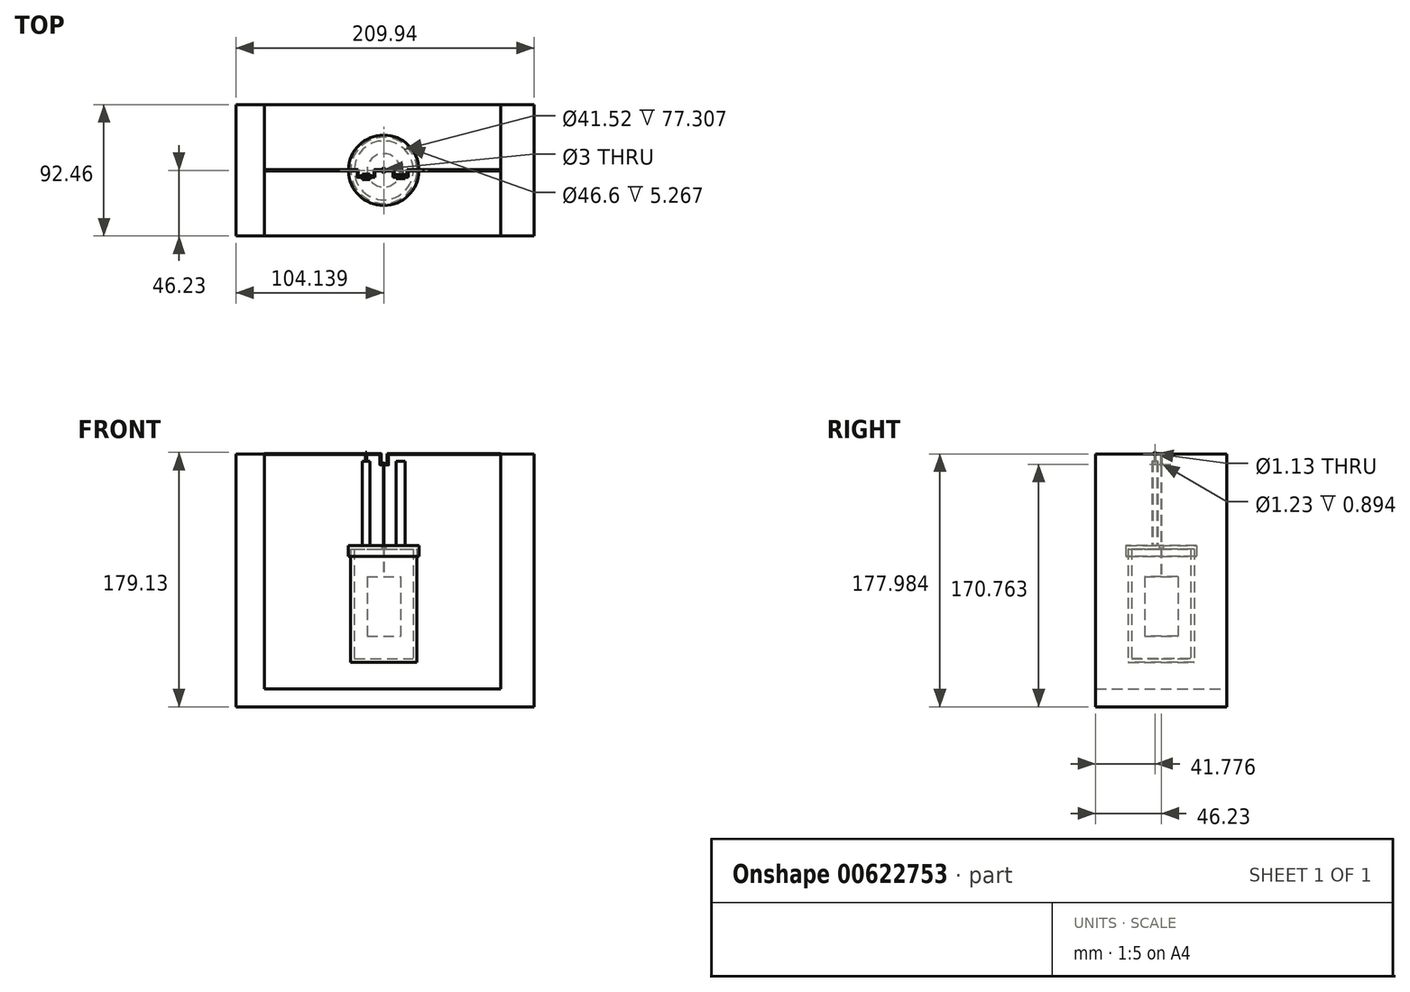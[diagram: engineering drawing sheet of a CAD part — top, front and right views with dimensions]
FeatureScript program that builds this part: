
annotation { "Feature Type Name" : "Feature", "Feature Type Description" : "" }
export const myFeature = defineFeature(function(context is Context, id is Id, definition is map)
    precondition{}
    {
        {
            var Q0;
            Q0=qCreatedBy(makeId("Front.planeOp"),FACE);
            var sketch = newSketch(context, id + "F0", { "sketchPlane" : qUnion([Q0])});
            skLineSegment(sketch, "E0.bottom", {"start": v(0, 0) * mm, "end": v(46.6, 0) * mm});
            skLineSegment(sketch, "E0.top", {"start": v(-1.54, 82.39) * mm, "end": v(43.64, 82.39) * mm});
            skLineSegment(sketch, "E0.left", {"start": v(0, 0) * mm, "end": v(0, 79.85) * mm});
            skLineSegment(sketch, "E0.right", {"start": v(46.6, 0) * mm, "end": v(46.6, 79.85) * mm});
            skLineSegment(sketch, "E1.0", {"start": v(2.54, 79.85) * mm, "end": v(44.06, 79.85) * mm});
            skLineSegment(sketch, "E1.1", {"start": v(2.54, 2.54) * mm, "end": v(2.54, 79.85) * mm});
            skLineSegment(sketch, "E1.2", {"start": v(2.54, 2.54) * mm, "end": v(44.06, 2.54) * mm});
            skLineSegment(sketch, "E1.3", {"start": v(44.06, 2.54) * mm, "end": v(44.06, 79.85) * mm});
            skLineSegment(sketch, "E2", {"start": v(21.8, 79.85) * mm, "end": v(21.8, 82.39) * mm});
            skLineSegment(sketch, "E3", {"start": v(25.2, 79.85) * mm, "end": v(25.2, 82.39) * mm});
            skLineSegment(sketch, "E4.bottom", {"start": v(11.55, 60.37) * mm, "end": v(35.83, 60.37) * mm});
            skLineSegment(sketch, "E4.top", {"start": v(11.55, 18.32) * mm, "end": v(35.83, 18.32) * mm});
            skLineSegment(sketch, "E4.left", {"start": v(11.55, 60.37) * mm, "end": v(11.55, 18.32) * mm});
            skLineSegment(sketch, "E4.right", {"start": v(35.83, 60.37) * mm, "end": v(35.83, 18.32) * mm});
            skLineSegment(sketch, "E5", {"start": v(23.1, 60.37) * mm, "end": v(23.1, 138.5) * mm});
            skLineSegment(sketch, "E6", {"start": v(23.5, 60.37) * mm, "end": v(23.5, 138.5) * mm});
            skLineSegment(sketch, "E7", {"start": v(23.5, 138.5) * mm, "end": v(23.1, 138.5) * mm});
            skLineSegment(sketch, "E8", {"start": v(2.54, 79.85) * mm, "end": v(0, 79.85) * mm});
            skLineSegment(sketch, "E9", {"start": v(44.06, 79.85) * mm, "end": v(46.6, 79.85) * mm});
            skLineSegment(sketch, "E10", {"start": v(-1.54, 82.39) * mm, "end": v(-1.54, 74.58) * mm});
            skLineSegment(sketch, "E11", {"start": v(-1.54, 74.58) * mm, "end": v(0, 74.58) * mm});
            skLineSegment(sketch, "E12", {"start": v(43.64, 82.39) * mm, "end": v(49.58, 82.39) * mm});
            skLineSegment(sketch, "E13", {"start": v(49.58, 82.39) * mm, "end": v(49.58, 75.33) * mm});
            skLineSegment(sketch, "E14", {"start": v(49.58, 75.33) * mm, "end": v(46.6, 75.33) * mm});
            skLineSegment(sketch, "E15", {"start": v(23.3, 0) * mm, "end": v(23.3, 138.5) * mm});
            skLineSegment(sketch, "E16", {"start": v(23.3, 139.45) * mm, "end": v(21, 139.45) * mm});
            skLineSegment(sketch, "E17", {"start": v(21, 139.45) * mm, "end": v(21, 146.67) * mm});
            skLineSegment(sketch, "E18", {"start": v(21, 146.67) * mm, "end": v(16.7, 146.67) * mm});
            skLineSegment(sketch, "E19", {"start": v(23.3, 139.45) * mm, "end": v(26.2, 139.45) * mm});
            skLineSegment(sketch, "E20", {"start": v(26.2, 139.45) * mm, "end": v(26.2, 146.67) * mm});
            skLineSegment(sketch, "E21", {"start": v(26.2, 146.67) * mm, "end": v(30.21, 146.67) * mm});
            skLineSegment(sketch, "E22", {"start": v(-60.88, 146.67) * mm, "end": v(-60.88, -18.58) * mm});
            skLineSegment(sketch, "E23", {"start": v(-60.88, -18.58) * mm, "end": v(105.66, -18.58) * mm});
            skLineSegment(sketch, "E24", {"start": v(105.66, -18.58) * mm, "end": v(105.66, 146.67) * mm});
            skLineSegment(sketch, "E25", {"start": v(105.66, 146.67) * mm, "end": v(129.1, 146.67) * mm});
            skLineSegment(sketch, "E26", {"start": v(129.1, 146.67) * mm, "end": v(129.1, -31.3) * mm});
            skLineSegment(sketch, "E27", {"start": v(129.1, -31.3) * mm, "end": v(-80.84, -31.3) * mm});
            skLineSegment(sketch, "E28", {"start": v(-80.84, -31.3) * mm, "end": v(-80.84, 146.67) * mm});
            skLineSegment(sketch, "E29", {"start": v(-80.84, 146.67) * mm, "end": v(-60.88, 146.67) * mm});
            skSolve(sketch);
        }
        {
            var Q0;
            Q0=sQuery(id+"F0.wireOp",EDGE,"E17");
            var Q1;
            Q1=sQuery(id+"F0.wireOp",VERTEX,"E18.start");
            cPlane(context, id + "F1", {"entities" : qUnion([Q0, Q1]), "cplaneType" : CPlaneType.LINE_POINT, "offset" : 25.4 * mm, "width" : 152.4 * mm, "height" : 152.4 * mm});
        }
        {
            var Q0;
            Q0=qCreatedBy(id+"F1.planeOp",FACE);
            var sketch = newSketch(context, id + "F2", { "sketchPlane" : qUnion([Q0])});
            skLineSegment(sketch, "E30", {"start": v(5.01, 0) * mm, "end": v(5.01, -4.45) * mm});
            skLineSegment(sketch, "E31", {"start": v(5.01, -4.45) * mm, "end": v(16.7, -4.45) * mm});
            skLineSegment(sketch, "E32", {"start": v(16.7, -4.45) * mm, "end": v(16.7, 0) * mm});
            skLineSegment(sketch, "E33", {"start": v(30.21, 0) * mm, "end": v(30.21, -4.45) * mm});
            skLineSegment(sketch, "E34", {"start": v(30.21, -4.45) * mm, "end": v(40.1, -4.45) * mm});
            skLineSegment(sketch, "E35", {"start": v(40.1, -4.45) * mm, "end": v(40.1, 0) * mm});
            skLineSegment(sketch, "E36", {"start": v(5.01, 0) * mm, "end": v(-60.88, 0) * mm});
            skLineSegment(sketch, "E37", {"start": v(40.1, 0) * mm, "end": v(105.66, 0) * mm});
            skSolve(sketch);
        }
        {
            var Q0;
            Q0=sQuery(id+"F2.wireOp",EDGE,"E36");
            var Q1;
            Q1=sQuery(id+"F2.wireOp",VERTEX,"E36.end");
            cPlane(context, id + "F3", {"entities" : qUnion([Q0, Q1]), "cplaneType" : CPlaneType.LINE_POINT, "offset" : 25.4 * mm, "width" : 152.4 * mm, "height" : 152.4 * mm});
        }
        {
            var Q0;
            Q0=qCreatedBy(id+"F3.planeOp",FACE);
            var sketch = newSketch(context, id + "F4", { "sketchPlane" : qUnion([Q0])});
            skCircle(sketch, "E38", {"center": v(0, 146.67) * mm, "radius": 0.44 * mm});
            skSolve(sketch);
        }
        {
            var Q0;
            {var subQ3=sQuery(id+"F0.wireOp",EDGE,"E1.1");Q0=makeQuery(id+"F0.imprint","IMPRINT",FACE,{"disambiguationData":[TD([[makeQuery(id+"F0.imprint","IMPRINT",EDGE,{"derivedFrom":subQ3}),1.0]])]});}
            var Q1;
            Q1=sQuery(id+"F0.wireOp",EDGE,"E15");
            revolve(context, id + "F5", {"entities" : qUnion([Q0]), "axis" : qUnion([Q1]), "revolveType" : RevolveType.FULL});
        }
        {
            var Q0;
            {var subQ4=sQuery(id+"F0.wireOp",EDGE,"E2");Q0=makeQuery(id+"F0.imprint","IMPRINT",FACE,{"disambiguationData":[TD([[makeQuery(id+"F0.imprint","IMPRINT",EDGE,{"derivedFrom":subQ4}),1.0]])]});}
            var Q1;
            Q1=sQuery(id+"F0.wireOp",EDGE,"E15");
            revolve(context, id + "F6", {"entities" : qUnion([Q0]), "axis" : qUnion([Q1]), "revolveType" : RevolveType.FULL});
        }
        {
            var Q0;
            {var subQ0=sQuery(id+"F0.wireOp",EDGE,"E4.left");Q0=makeQuery(id+"F0.imprint","IMPRINT",FACE,{"disambiguationData":[TD([[makeQuery(id+"F0.imprint","IMPRINT",EDGE,{"derivedFrom":subQ0}),1.0]])]});}
            var Q1;
            Q1=sQuery(id+"F0.wireOp",EDGE,"E15");
            revolve(context, id + "F7", {"entities" : qUnion([Q0]), "axis" : qUnion([Q1]), "revolveType" : RevolveType.FULL});
        }
        {
            var Q0;
            {var subQ0=sQuery(id+"F0.wireOp",EDGE,"E5");var subQ1=sQuery(id+"F0.wireOp",EDGE,"E0.top");var subQ2=makeQuery(id+"F0.imprint","INTERSECT",VERTEX,{"derivedFrom":[subQ1,subQ0]});Q0=makeQuery(id+"F0.imprint","IMPRINT",FACE,{"disambiguationData":[TD([[makeQuery(id+"F0.imprint","IMPRINT",EDGE,{"disambiguationData":[TD([[subQ2,-1.0]])],"derivedFrom":subQ1}),1.0]])]});}
            var Q1;
            {var subQ0=sQuery(id+"F0.wireOp",EDGE,"E5");var subQ1=sQuery(id+"F0.wireOp",EDGE,"E0.top");var subQ2=makeQuery(id+"F0.imprint","INTERSECT",VERTEX,{"derivedFrom":[subQ1,subQ0]});Q1=makeQuery(id+"F0.imprint","IMPRINT",FACE,{"disambiguationData":[TD([[makeQuery(id+"F0.imprint","IMPRINT",EDGE,{"disambiguationData":[TD([[subQ2,-1.0]])],"derivedFrom":subQ1}),-1.0]])]});}
            var Q2;
            {var subQ0=sQuery(id+"F0.wireOp",EDGE,"E5");var subQ1=sQuery(id+"F0.wireOp",EDGE,"E1.0");var subQ2=makeQuery(id+"F0.imprint","INTERSECT",VERTEX,{"derivedFrom":[subQ1,subQ0]});Q2=makeQuery(id+"F0.imprint","IMPRINT",FACE,{"disambiguationData":[TD([[makeQuery(id+"F0.imprint","IMPRINT",EDGE,{"disambiguationData":[TD([[subQ2,-1.0]])],"derivedFrom":subQ1}),-1.0]])]});}
            var Q3;
            Q3=sQuery(id+"F0.wireOp",EDGE,"E15");
            revolve(context, id + "F8", {"entities" : qUnion([Q0, Q1, Q2]), "axis" : qUnion([Q3]), "revolveType" : RevolveType.FULL});
        }
        {
            var Q0;
            Q0=makeQuery(id+"F4.imprint","IMPRINT",FACE,{"disambiguationData":[TD([[makeQuery(id+"F4.imprint","IMPRINT",EDGE,{"derivedFrom":sQuery(id+"F4.wireOp",EDGE,"E38")}),1.0]])]});
            var Q1;
            Q1=sQuery(id+"F2.wireOp",EDGE,"E36");
            var Q2;
            Q2=sQuery(id+"F2.wireOp",EDGE,"E30");
            var Q3;
            Q3=sQuery(id+"F2.wireOp",EDGE,"E31");
            var Q4;
            Q4=sQuery(id+"F2.wireOp",EDGE,"E35");
            var Q5;
            Q5=sQuery(id+"F2.wireOp",EDGE,"E34");
            var Q6;
            Q6=sQuery(id+"F2.wireOp",EDGE,"E33");
            var Q7;
            Q7=sQuery(id+"F0.wireOp",EDGE,"E21");
            var Q8;
            Q8=sQuery(id+"F2.wireOp",EDGE,"E37");
            var Q9;
            Q9=sQuery(id+"F0.wireOp",EDGE,"E20");
            var Q10;
            Q10=sQuery(id+"F0.wireOp",EDGE,"E17");
            var Q11;
            Q11=sQuery(id+"F0.wireOp",EDGE,"E16");
            var Q12;
            Q12=sQuery(id+"F0.wireOp",EDGE,"E19");
            var Q13;
            Q13=sQuery(id+"F2.wireOp",EDGE,"E32");
            var Q14;
            Q14=sQuery(id+"F0.wireOp",EDGE,"E18");
            sweep(context, id + "F9", {"profiles" : qUnion([Q0]), "path" : qUnion([Q1, Q2, Q3, Q4, Q5, Q6, Q7, Q8, Q9, Q10, Q11, Q12, Q13, Q14])});
        }
        {
            var Q0;
            Q0=sQuery(id+"F0.wireOp",EDGE,"E10");
            var Q1;
            Q1=sQuery(id+"F0.wireOp",VERTEX,"E10.start");
            cPlane(context, id + "F10", {"entities" : qUnion([Q0, Q1]), "cplaneType" : CPlaneType.LINE_POINT, "offset" : 25.4 * mm, "width" : 152.4 * mm, "height" : 152.4 * mm});
        }
        {
            var Q0;
            Q0=qCreatedBy(id+"F10.planeOp",FACE);
            var sketch = newSketch(context, id + "F11", { "sketchPlane" : qUnion([Q0])});
            skLineSegment(sketch, "E39.bottom", {"start": v(13.46, 2.54) * mm, "end": v(8.26, 2.54) * mm});
            skLineSegment(sketch, "E39.top", {"start": v(13.46, 6.37) * mm, "end": v(8.26, 6.37) * mm});
            skLineSegment(sketch, "E39.left", {"start": v(13.46, 2.54) * mm, "end": v(13.46, 6.37) * mm});
            skLineSegment(sketch, "E39.right", {"start": v(8.26, 2.54) * mm, "end": v(8.26, 6.37) * mm});
            skPoint(sketch, "E39.middle", {"position": v(10.86, 4.45) * mm});
            skLineSegment(sketch, "E40.bottom", {"start": v(38.3, 5.98) * mm, "end": v(32.01, 5.98) * mm});
            skLineSegment(sketch, "E40.top", {"start": v(38.3, 2.93) * mm, "end": v(32.01, 2.93) * mm});
            skLineSegment(sketch, "E40.left", {"start": v(38.3, 5.98) * mm, "end": v(38.3, 2.93) * mm});
            skLineSegment(sketch, "E40.right", {"start": v(32.01, 5.98) * mm, "end": v(32.01, 2.93) * mm});
            skPoint(sketch, "E40.middle", {"position": v(35.16, 4.45) * mm});
            skSolve(sketch);
        }
        {
            var Q0;
            Q0=makeQuery(id+"F11.imprint","IMPRINT",FACE,{"disambiguationData":[TD([[makeQuery(id+"F11.imprint","IMPRINT",EDGE,{"derivedFrom":sQuery(id+"F11.wireOp",EDGE,"E39.bottom")}),-1.0]])]});
            var Q1;
            Q1=makeQuery(id+"F11.imprint","IMPRINT",FACE,{"disambiguationData":[TD([[makeQuery(id+"F11.imprint","IMPRINT",EDGE,{"derivedFrom":sQuery(id+"F11.wireOp",EDGE,"E40.bottom")}),1.0]])]});
            extrude(context, id + "F12", {"entities" : qUnion([Q0, Q1]), "oppositeDirection" : true, "depth" : 59.26 * mm, "offsetDistance" : 25.4 * mm});
        }
        {
            var Q0;
            Q0=sQuery(id+"F0.wireOp",EDGE,"E7");
            var Q1;
            Q1=sQuery(id+"F0.wireOp",VERTEX,"E15.end");
            cPlane(context, id + "F13", {"entities" : qUnion([Q0, Q1]), "cplaneType" : CPlaneType.LINE_POINT, "offset" : 25.4 * mm, "width" : 152.4 * mm, "height" : 152.4 * mm});
        }
        {
            var Q0;
            Q0=qCreatedBy(id+"F13.planeOp",FACE);
            var sketch = newSketch(context, id + "F14", { "sketchPlane" : qUnion([Q0])});
            skCircle(sketch, "E41", {"center": v(0, 139.45) * mm, "radius": 0.62 * mm});
            skCircle(sketch, "E42.0", {"center": v(0, 139.45) * mm, "radius": 0.95 * mm});
            skLineSegment(sketch, "E43", {"start": v(-0.34, 138.57) * mm, "end": v(-0.16, 138.22) * mm});
            skLineSegment(sketch, "E44", {"start": v(-0.16, 138.22) * mm, "end": v(0.13, 138.22) * mm});
            skLineSegment(sketch, "E45", {"start": v(0.13, 138.22) * mm, "end": v(0.3, 138.55) * mm});
            skSolve(sketch);
        }
        {
            var Q0;
            Q0 = qSketchRegion(id + "F14", true);
            extrude(context, id + "F15", {"entities" : qUnion([Q0]), "operationType" : NewBodyOperationType.ADD, "endBound" : BoundingType.SYMMETRIC, "oppositeDirection" : true, "depth" : 0.9 * mm, "offsetDistance" : 25.4 * mm});
        }
        {
            var Q0;
            Q0=sQuery(id+"F2.wireOp",EDGE,"E31");
            cPoint(context, id + "F16", {"entities" : qUnion([Q0]), "parameter" : 0.5});
        }
        {
            var Q0;
            Q0 = qCreatedBy(id + "F16" ,VERTEX);
            var Q1;
            Q1=sQuery(id+"F2.wireOp",EDGE,"E31");
            cPlane(context, id + "F17", {"entities" : qUnion([Q0, Q1]), "cplaneType" : CPlaneType.LINE_POINT, "offset" : 25.4 * mm, "width" : 152.4 * mm, "height" : 152.4 * mm});
        }
        {
            var Q0;
            Q0=qCreatedBy(id+"F17.planeOp",FACE);
            var sketch = newSketch(context, id + "F18", { "sketchPlane" : qUnion([Q0])});
            skCircle(sketch, "E46", {"center": v(-4.45, 146.67) * mm, "radius": 0.56 * mm});
            skCircle(sketch, "E47.0", {"center": v(-4.45, 146.67) * mm, "radius": 1.15 * mm});
            skSolve(sketch);
        }
        {
            var Q0;
            Q0=makeQuery(id+"F18.imprint","IMPRINT",FACE,{"disambiguationData":[TD([[makeQuery(id+"F18.imprint","IMPRINT",EDGE,{"derivedFrom":sQuery(id+"F18.wireOp",EDGE,"E46")}),-1.0]])]});
            extrude(context, id + "F19", {"entities" : qUnion([Q0]), "endBound" : BoundingType.SYMMETRIC, "oppositeDirection" : true, "depth" : 0.71 * mm, "offsetDistance" : 25.4 * mm});
        }
        {
            var Q0;
            Q0=makeQuery(id+"F12.opExtrude","CAP_FACE",FACE,{"disambiguationData":[OSD([sQuery(id+"F11.wireOp",EDGE,"E39.bottom"),sQuery(id+"F11.wireOp",EDGE,"E39.top"),sQuery(id+"F11.wireOp",EDGE,"E39.left"),sQuery(id+"F11.wireOp",EDGE,"E39.right")])],"isStart":false});
            var sketch = newSketch(context, id + "F20", { "sketchPlane" : qUnion([Q0])});
            skCircle(sketch, "E48", {"center": v(10.86, -4.45) * mm, "radius": 0.39 * mm});
            skSolve(sketch);
        }
        {
            var Q0;
            Q0 = qSketchRegion(id + "F20", true);
            extrude(context, id + "F21", {"entities" : qUnion([Q0]), "operationType" : NewBodyOperationType.ADD, "depth" : 4.27 * mm, "offsetDistance" : 25.4 * mm});
        }
        {
            var Q0;
            Q0=makeQuery(id+"F0.imprint","IMPRINT",FACE,{"disambiguationData":[TD([[makeQuery(id+"F0.imprint","IMPRINT",EDGE,{"derivedFrom":sQuery(id+"F0.wireOp",EDGE,"E22")}),-1.0]])]});
            extrude(context, id + "F22", {"entities" : qUnion([Q0]), "endBound" : BoundingType.SYMMETRIC, "depth" : 92.46 * mm, "offsetDistance" : 25.4 * mm});
        }
    });
